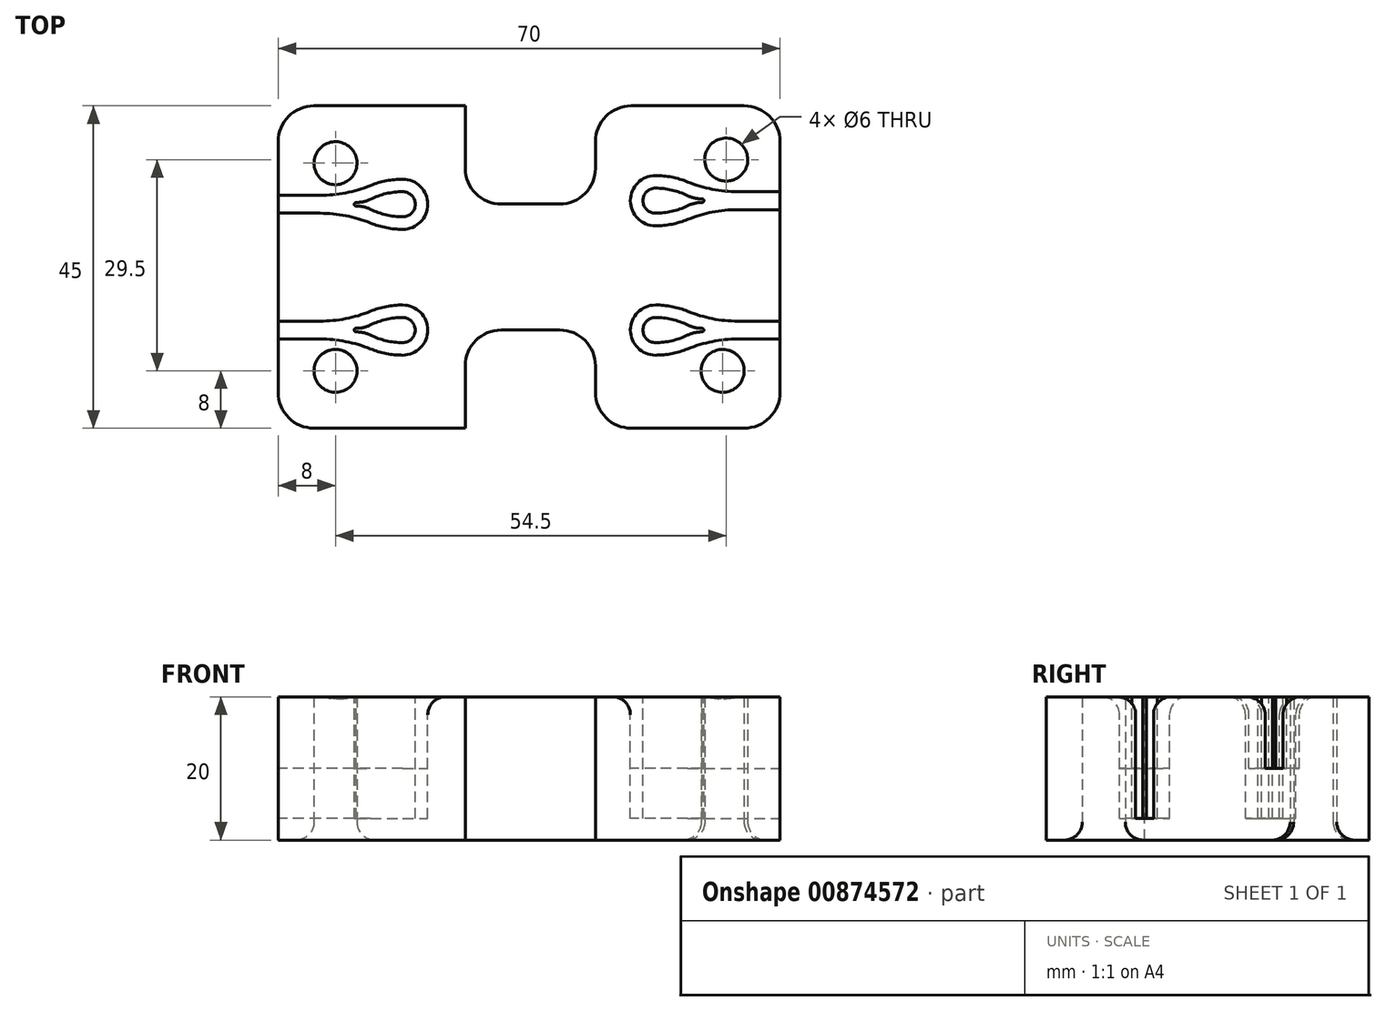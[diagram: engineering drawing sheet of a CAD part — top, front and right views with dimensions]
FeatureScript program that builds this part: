
annotation { "Feature Type Name" : "Feature", "Feature Type Description" : "" }
export const myFeature = defineFeature(function(context is Context, id is Id, definition is map)
    precondition{}
    {
        {
            var Q0;
            Q0=qCreatedBy(makeId("Top.planeOp"),FACE);
            var sketch = newSketch(context, id + "F0", { "sketchPlane" : qUnion([Q0])});
            skLineSegment(sketch, "E0.bottom", {"start": v(-35, 22.5) * mm, "end": v(35, 22.5) * mm});
            skLineSegment(sketch, "E0.top", {"start": v(-35, -22.5) * mm, "end": v(35, -22.5) * mm});
            skLineSegment(sketch, "E0.left", {"start": v(-35, 22.5) * mm, "end": v(-35, -22.5) * mm});
            skLineSegment(sketch, "E0.right", {"start": v(35, 22.5) * mm, "end": v(35, -22.5) * mm});
            skCircle(sketch, "E1", {"center": v(-27, 14.5) * mm, "radius": 3 * mm});
            skCircle(sketch, "E2", {"center": v(-27, -14.5) * mm, "radius": 3 * mm});
            skCircle(sketch, "E3", {"center": v(27, -14.5) * mm, "radius": 3 * mm});
            skCircle(sketch, "E4", {"center": v(27.5, 15) * mm, "radius": 3 * mm});
            skSolve(sketch);
        }
        {
            var Q0;
            Q0=makeQuery(id+"F0.imprint","IMPRINT",FACE,{"disambiguationData":[TD([[makeQuery(id+"F0.imprint","IMPRINT",EDGE,{"derivedFrom":sQuery(id+"F0.wireOp",EDGE,"E0.bottom")}),-1.0]])]});
            var Q1;
            Q1 = qSketchRegion(id + "F0", true);
            extrude(context, id + "F1", {"entities" : qUnion([Q0, Q1]), "depth" : 20 * mm, "offsetDistance" : 25 * mm});
        }
        {
            var Q0;
            Q0=makeQuery(id+"F1.opExtrude","CAP_FACE",FACE,{"disambiguationData":[OSD([sQuery(id+"F0.wireOp",EDGE,"E0.bottom"),sQuery(id+"F0.wireOp",EDGE,"E0.top"),sQuery(id+"F0.wireOp",EDGE,"E0.left"),sQuery(id+"F0.wireOp",EDGE,"E0.right"),sQuery(id+"F0.wireOp",EDGE,"E1"),sQuery(id+"F0.wireOp",EDGE,"E2"),sQuery(id+"F0.wireOp",EDGE,"E3"),sQuery(id+"F0.wireOp",EDGE,"E4")])],"isStart":false});
            var sketch = newSketch(context, id + "F2", { "sketchPlane" : qUnion([Q0])});
            skArc(sketch, "E5", {"start": v(17.63, 12.76) * mm, "mid": v(14.13, 9.26) * mm, "end": v(17.63, 5.76) * mm});
            skArc(sketch, "E6", {"start": v(17.63, 12.76) * mm, "mid": v(19.92, 12.54) * mm, "end": v(22.13, 11.88) * mm});
            skArc(sketch, "E7", {"start": v(22.13, 11.88) * mm, "mid": v(25.56, 10.86) * mm, "end": v(29.13, 10.51) * mm});
            skArc(sketch, "E8", {"start": v(17.63, 5.76) * mm, "mid": v(19.92, 5.98) * mm, "end": v(22.13, 6.64) * mm});
            skArc(sketch, "E9", {"start": v(22.13, 6.64) * mm, "mid": v(25.56, 7.67) * mm, "end": v(29.13, 8.01) * mm});
            skArc(sketch, "E10.0", {"start": v(17.63, 7.51) * mm, "mid": v(19.94, 7.78) * mm, "end": v(22.13, 8.56) * mm});
            skArc(sketch, "E10.1", {"start": v(17.63, 11.01) * mm, "mid": v(15.88, 9.26) * mm, "end": v(17.63, 7.51) * mm});
            skArc(sketch, "E10.4", {"start": v(17.63, 11.01) * mm, "mid": v(19.94, 10.75) * mm, "end": v(22.13, 9.96) * mm});
            skArc(sketch, "E11", {"start": v(22.13, 9.96) * mm, "mid": v(23.1, 9.62) * mm, "end": v(24.13, 9.51) * mm});
            skArc(sketch, "E12", {"start": v(22.13, 8.56) * mm, "mid": v(23.1, 8.9) * mm, "end": v(24.13, 9.01) * mm});
            skArc(sketch, "E13", {"start": v(24.13, 9.01) * mm, "mid": v(24.38, 9.26) * mm, "end": v(24.13, 9.51) * mm});
            skLineSegment(sketch, "E14.bottom", {"start": v(29.13, 10.51) * mm, "end": v(35, 10.51) * mm});
            skLineSegment(sketch, "E14.top", {"start": v(29.13, 8.01) * mm, "end": v(35, 8.01) * mm});
            skLineSegment(sketch, "E14.right", {"start": v(35, 10.51) * mm, "end": v(35, 8.01) * mm});
            skArc(sketch, "E15", {"start": v(17.63, -5.3) * mm, "mid": v(14.13, -8.8) * mm, "end": v(17.63, -12.3) * mm});
            skArc(sketch, "E16", {"start": v(17.63, -5.3) * mm, "mid": v(19.92, -5.52) * mm, "end": v(22.13, -6.18) * mm});
            skArc(sketch, "E17", {"start": v(22.13, -6.18) * mm, "mid": v(25.56, -7.2) * mm, "end": v(29.13, -7.55) * mm});
            skArc(sketch, "E18", {"start": v(17.63, -12.3) * mm, "mid": v(19.92, -12.08) * mm, "end": v(22.13, -11.42) * mm});
            skArc(sketch, "E19", {"start": v(22.13, -11.42) * mm, "mid": v(25.56, -10.4) * mm, "end": v(29.13, -10.05) * mm});
            skArc(sketch, "E20.0", {"start": v(17.63, -10.55) * mm, "mid": v(19.94, -10.29) * mm, "end": v(22.13, -9.5) * mm});
            skArc(sketch, "E20.1", {"start": v(17.63, -7.05) * mm, "mid": v(15.88, -8.8) * mm, "end": v(17.63, -10.55) * mm});
            skArc(sketch, "E20.4", {"start": v(17.63, -7.05) * mm, "mid": v(19.94, -7.32) * mm, "end": v(22.13, -8.1) * mm});
            skArc(sketch, "E21", {"start": v(22.13, -8.1) * mm, "mid": v(23.1, -8.44) * mm, "end": v(24.13, -8.55) * mm});
            skArc(sketch, "E22", {"start": v(22.13, -9.5) * mm, "mid": v(23.1, -9.16) * mm, "end": v(24.13, -9.05) * mm});
            skArc(sketch, "E23", {"start": v(24.13, -9.05) * mm, "mid": v(24.38, -8.8) * mm, "end": v(24.13, -8.55) * mm});
            skLineSegment(sketch, "E24.bottom", {"start": v(29.13, -7.55) * mm, "end": v(35, -7.55) * mm});
            skLineSegment(sketch, "E24.top", {"start": v(29.13, -10.05) * mm, "end": v(35, -10.05) * mm});
            skLineSegment(sketch, "E24.right", {"start": v(35, -7.55) * mm, "end": v(35, -10.05) * mm});
            skArc(sketch, "E25", {"start": v(-17.64, -12.3) * mm, "mid": v(-14.14, -8.8) * mm, "end": v(-17.64, -5.3) * mm});
            skArc(sketch, "E26", {"start": v(-17.64, -12.3) * mm, "mid": v(-19.93, -12.08) * mm, "end": v(-22.14, -11.42) * mm});
            skArc(sketch, "E27", {"start": v(-22.14, -11.42) * mm, "mid": v(-25.57, -10.4) * mm, "end": v(-29.14, -10.05) * mm});
            skArc(sketch, "E28", {"start": v(-17.64, -5.3) * mm, "mid": v(-19.93, -5.52) * mm, "end": v(-22.14, -6.18) * mm});
            skArc(sketch, "E29", {"start": v(-22.14, -6.18) * mm, "mid": v(-25.57, -7.2) * mm, "end": v(-29.14, -7.55) * mm});
            skArc(sketch, "E30.0", {"start": v(-17.64, -7.05) * mm, "mid": v(-19.95, -7.32) * mm, "end": v(-22.14, -8.1) * mm});
            skArc(sketch, "E30.1", {"start": v(-17.64, -10.55) * mm, "mid": v(-15.89, -8.8) * mm, "end": v(-17.64, -7.05) * mm});
            skArc(sketch, "E30.4", {"start": v(-17.64, -10.55) * mm, "mid": v(-19.95, -10.29) * mm, "end": v(-22.14, -9.5) * mm});
            skArc(sketch, "E31", {"start": v(-22.14, -9.5) * mm, "mid": v(-23.1, -9.16) * mm, "end": v(-24.13, -9.05) * mm});
            skArc(sketch, "E32", {"start": v(-22.14, -8.1) * mm, "mid": v(-23.11, -8.44) * mm, "end": v(-24.14, -8.55) * mm});
            skArc(sketch, "E33", {"start": v(-24.14, -8.55) * mm, "mid": v(-24.39, -8.8) * mm, "end": v(-24.13, -9.05) * mm});
            skLineSegment(sketch, "E34.bottom", {"start": v(-29.14, -10.05) * mm, "end": v(-35, -10.05) * mm});
            skLineSegment(sketch, "E34.top", {"start": v(-29.14, -7.55) * mm, "end": v(-35, -7.55) * mm});
            skLineSegment(sketch, "E34.right", {"start": v(-35, -10.05) * mm, "end": v(-35, -7.55) * mm});
            skArc(sketch, "E35", {"start": v(-17.63, 5.26) * mm, "mid": v(-14.13, 8.76) * mm, "end": v(-17.63, 12.26) * mm});
            skArc(sketch, "E36", {"start": v(-17.63, 5.26) * mm, "mid": v(-19.92, 5.48) * mm, "end": v(-22.13, 6.14) * mm});
            skArc(sketch, "E37", {"start": v(-22.13, 6.14) * mm, "mid": v(-25.56, 7.17) * mm, "end": v(-29.13, 7.51) * mm});
            skArc(sketch, "E38", {"start": v(-17.63, 12.26) * mm, "mid": v(-19.92, 12.04) * mm, "end": v(-22.13, 11.38) * mm});
            skArc(sketch, "E39", {"start": v(-22.13, 11.38) * mm, "mid": v(-25.56, 10.36) * mm, "end": v(-29.13, 10.01) * mm});
            skArc(sketch, "E40.0", {"start": v(-17.63, 10.51) * mm, "mid": v(-19.94, 10.25) * mm, "end": v(-22.13, 9.46) * mm});
            skArc(sketch, "E40.1", {"start": v(-17.63, 7.01) * mm, "mid": v(-15.88, 8.76) * mm, "end": v(-17.63, 10.51) * mm});
            skArc(sketch, "E40.4", {"start": v(-17.63, 7.01) * mm, "mid": v(-19.94, 7.28) * mm, "end": v(-22.13, 8.06) * mm});
            skArc(sketch, "E41", {"start": v(-22.13, 8.06) * mm, "mid": v(-23.1, 8.4) * mm, "end": v(-24.13, 8.51) * mm});
            skArc(sketch, "E42", {"start": v(-22.13, 9.46) * mm, "mid": v(-23.1, 9.12) * mm, "end": v(-24.13, 9.01) * mm});
            skArc(sketch, "E43", {"start": v(-24.13, 9.01) * mm, "mid": v(-24.38, 8.76) * mm, "end": v(-24.13, 8.51) * mm});
            skLineSegment(sketch, "E44.bottom", {"start": v(-29.13, 7.51) * mm, "end": v(-35, 7.51) * mm});
            skLineSegment(sketch, "E44.top", {"start": v(-29.13, 10.01) * mm, "end": v(-35, 10.01) * mm});
            skLineSegment(sketch, "E44.right", {"start": v(-35, 7.51) * mm, "end": v(-35, 10.01) * mm});
            skSolve(sketch);
        }
        {
            var Q0;
            {var subQ0=sQuery(id+"F0.wireOp",EDGE,"E0.top");var subQ1=sQuery(id+"F0.wireOp",EDGE,"E0.right");var subQ2=sQuery(id+"F0.wireOp",EDGE,"E0.bottom");var subQ3=sQuery(id+"F0.wireOp",EDGE,"E1");var subQ4=sQuery(id+"F0.wireOp",EDGE,"E2");var subQ5=sQuery(id+"F0.wireOp",EDGE,"E3");var subQ6=sQuery(id+"F0.wireOp",EDGE,"E4");var subQ7=sQuery(id+"F0.wireOp",EDGE,"E0.left");Q0=makeQuery(id+"FxYTic0K67xtiS1_1.boolean.opBoolean","SPLIT",FACE,{"disambiguationData":[TD([makeQuery(id+"F1.opExtrude","SWEPT_FACE",FACE,{"disambiguationData":[OSD([subQ2])]})])],"derivedFrom":makeQuery(id+"F1.opExtrude","CAP_FACE",FACE,{"disambiguationData":[OSD([subQ2,subQ0,subQ7,subQ1,subQ3,subQ4,subQ5,subQ6])],"isStart":false})});}
            var sketch = newSketch(context, id + "F3", { "sketchPlane" : qUnion([Q0])});
            skLineSegment(sketch, "E45.bottom", {"start": v(-8.9, 22.5) * mm, "end": v(9.26, 22.5) * mm});
            skLineSegment(sketch, "E45.top", {"start": v(-8.9, 8.8) * mm, "end": v(9.26, 8.8) * mm});
            skLineSegment(sketch, "E45.left", {"start": v(-8.9, 22.5) * mm, "end": v(-8.9, 8.8) * mm});
            skLineSegment(sketch, "E45.right", {"start": v(9.26, 22.5) * mm, "end": v(9.26, 8.8) * mm});
            skLineSegment(sketch, "E46.bottom", {"start": v(-8.9, -8.8) * mm, "end": v(9.26, -8.8) * mm});
            skLineSegment(sketch, "E46.top", {"start": v(-8.9, -22.5) * mm, "end": v(9.26, -22.5) * mm});
            skLineSegment(sketch, "E46.left", {"start": v(-8.9, -8.8) * mm, "end": v(-8.9, -22.5) * mm});
            skLineSegment(sketch, "E46.right", {"start": v(9.26, -8.8) * mm, "end": v(9.26, -22.5) * mm});
            skSolve(sketch);
        }
        {
            var Q0;
            Q0 = qSketchRegion(id + "F2", true);
            extrude(context, id + "F4", {"entities" : qUnion([Q0]), "operationType" : NewBodyOperationType.REMOVE, "oppositeDirection" : true, "depth" : 10 * mm, "offsetDistance" : 25 * mm});
        }
        {
            var Q0;
            Q0 = qSketchRegion(id + "F3", true);
            extrude(context, id + "F5", {"entities" : qUnion([Q0]), "operationType" : NewBodyOperationType.REMOVE, "oppositeDirection" : true, "depth" : 25 * mm, "offsetDistance" : 25 * mm});
        }
        {
            var Q0;
            Q0=makeQuery(id+"F5.boolean.opBoolean","COPY",EDGE,{"derivedFrom":makeQuery(id+"F5.opExtrude","SWEPT_EDGE",EDGE,{"disambiguationData":[OSD([sQuery(id+"F0.wireOp",EDGE,"E0.bottom"),sQuery(id+"F3.wireOp",EDGE,"E45.bottom"),sQuery(id+"F3.wireOp",EDGE,"E45.left")])]})});
            var Q1;
            Q1=makeQuery(id+"F5.boolean.opBoolean","COPY",EDGE,{"derivedFrom":makeQuery(id+"F5.opExtrude","SWEPT_EDGE",EDGE,{"disambiguationData":[OSD([sQuery(id+"F0.wireOp",EDGE,"E0.bottom"),sQuery(id+"F3.wireOp",EDGE,"E45.bottom"),sQuery(id+"F3.wireOp",EDGE,"E45.right")])]})});
            var Q2;
            Q2=makeQuery(id+"F1.opExtrude","SWEPT_EDGE",EDGE,{"disambiguationData":[OSD([sQuery(id+"F0.wireOp",EDGE,"E0.bottom"),sQuery(id+"F0.wireOp",EDGE,"E0.right")])]});
            var Q3;
            Q3=makeQuery(id+"F1.opExtrude","SWEPT_EDGE",EDGE,{"disambiguationData":[OSD([sQuery(id+"F0.wireOp",EDGE,"E0.top"),sQuery(id+"F0.wireOp",EDGE,"E0.right")])]});
            var Q4;
            Q4=makeQuery(id+"F5.boolean.opBoolean","COPY",EDGE,{"derivedFrom":makeQuery(id+"F5.opExtrude","SWEPT_EDGE",EDGE,{"disambiguationData":[OSD([sQuery(id+"F0.wireOp",EDGE,"E0.top"),sQuery(id+"F3.wireOp",EDGE,"E46.top"),sQuery(id+"F3.wireOp",EDGE,"E46.right")])]})});
            var Q5;
            Q5=makeQuery(id+"F5.boolean.opBoolean","COPY",EDGE,{"derivedFrom":makeQuery(id+"F5.opExtrude","SWEPT_EDGE",EDGE,{"disambiguationData":[OSD([sQuery(id+"F0.wireOp",EDGE,"E0.top"),sQuery(id+"F3.wireOp",EDGE,"E46.top"),sQuery(id+"F3.wireOp",EDGE,"E46.left")])]})});
            var Q6;
            Q6=makeQuery(id+"F1.opExtrude","SWEPT_EDGE",EDGE,{"disambiguationData":[OSD([sQuery(id+"F0.wireOp",EDGE,"E0.top"),sQuery(id+"F0.wireOp",EDGE,"E0.left")])]});
            var Q7;
            Q7=makeQuery(id+"F1.opExtrude","SWEPT_EDGE",EDGE,{"disambiguationData":[OSD([sQuery(id+"F0.wireOp",EDGE,"E0.bottom"),sQuery(id+"F0.wireOp",EDGE,"E0.left")])]});
            var Q8;
            Q8=makeQuery(id+"F5.boolean.opBoolean","COPY",EDGE,{"derivedFrom":makeQuery(id+"F5.opExtrude","SWEPT_EDGE",EDGE,{"disambiguationData":[OSD([sQuery(id+"F3.wireOp",EDGE,"E46.bottom"),sQuery(id+"F3.wireOp",EDGE,"E46.left")])]})});
            var Q9;
            Q9=makeQuery(id+"F5.boolean.opBoolean","COPY",EDGE,{"derivedFrom":makeQuery(id+"F5.opExtrude","SWEPT_EDGE",EDGE,{"disambiguationData":[OSD([sQuery(id+"F3.wireOp",EDGE,"E46.bottom"),sQuery(id+"F3.wireOp",EDGE,"E46.right")])]})});
            var Q10;
            Q10=makeQuery(id+"F5.boolean.opBoolean","COPY",EDGE,{"derivedFrom":makeQuery(id+"F5.opExtrude","SWEPT_EDGE",EDGE,{"disambiguationData":[OSD([sQuery(id+"F3.wireOp",EDGE,"E45.top"),sQuery(id+"F3.wireOp",EDGE,"E45.right")])]})});
            var Q11;
            Q11=makeQuery(id+"F5.boolean.opBoolean","COPY",EDGE,{"derivedFrom":makeQuery(id+"F5.opExtrude","SWEPT_EDGE",EDGE,{"disambiguationData":[OSD([sQuery(id+"F3.wireOp",EDGE,"E45.top"),sQuery(id+"F3.wireOp",EDGE,"E45.left")])]})});
            fillet(context, id + "F6", {"entities" : qUnion([Q0, Q1, Q2, Q3, Q4, Q5, Q6, Q7, Q8, Q9, Q10, Q11]), "radius" : 5 * mm, "tangentPropagation" : true, "allowEdgeOverflow" : false});
        }
        {
            var Q0;
            Q0=makeQuery(id+"F4.boolean.opBoolean","COPY",EDGE,{"derivedFrom":makeQuery(id+"F4.opExtrude","CAP_EDGE",EDGE,{"disambiguationData":[OSD([sQuery(id+"F2.wireOp",EDGE,"E44.top")])],"isStart":true})});
            var Q1;
            Q1=makeQuery(id+"F4.boolean.opBoolean","COPY",EDGE,{"derivedFrom":makeQuery(id+"F4.opExtrude","CAP_EDGE",EDGE,{"disambiguationData":[OSD([sQuery(id+"F2.wireOp",EDGE,"E14.bottom")])],"isStart":true})});
            var Q2;
            Q2=makeQuery(id+"F4.boolean.opBoolean","COPY",EDGE,{"derivedFrom":makeQuery(id+"F4.opExtrude","CAP_EDGE",EDGE,{"disambiguationData":[OSD([sQuery(id+"F2.wireOp",EDGE,"E24.bottom")])],"isStart":true})});
            var Q3;
            Q3=makeQuery(id+"F4.boolean.opBoolean","COPY",EDGE,{"derivedFrom":makeQuery(id+"F4.opExtrude","CAP_EDGE",EDGE,{"disambiguationData":[OSD([sQuery(id+"F2.wireOp",EDGE,"E28")])],"isStart":true})});
            fillet(context, id + "F7", {"entities" : qUnion([Q0, Q1, Q2, Q3]), "radius" : 2.5 * mm, "tangentPropagation" : true, "allowEdgeOverflow" : false});
        }
        {
            var Q0;
            Q0=makeQuery(id+"F1.opExtrude","CAP_EDGE",EDGE,{"disambiguationData":[OSD([sQuery(id+"F0.wireOp",EDGE,"E1")])],"isStart":true});
            var Q1;
            Q1=makeQuery(id+"F1.opExtrude","CAP_EDGE",EDGE,{"disambiguationData":[OSD([sQuery(id+"F0.wireOp",EDGE,"E2")])],"isStart":true});
            var Q2;
            Q2=makeQuery(id+"F1.opExtrude","CAP_EDGE",EDGE,{"disambiguationData":[OSD([sQuery(id+"F0.wireOp",EDGE,"E3")])],"isStart":true});
            var Q3;
            Q3=makeQuery(id+"F1.opExtrude","CAP_EDGE",EDGE,{"disambiguationData":[OSD([sQuery(id+"F0.wireOp",EDGE,"E4")])],"isStart":true});
            fillet(context, id + "F8", {"entities" : qUnion([Q0, Q1, Q2, Q3]), "radius" : 2.5 * mm, "tangentPropagation" : true, "allowEdgeOverflow" : false});
        }
        {
            var Q0;
            {var subQ5=sQuery(id+"F0.wireOp",EDGE,"E0.left");var subQ6=sQuery(id+"F0.wireOp",EDGE,"E0.top");Q0=makeQuery(id+"F5.boolean.opBoolean","SPLIT",FACE,{"disambiguationData":[TD([makeQuery(id+"F1.opExtrude","SWEPT_FACE",FACE,{"disambiguationData":[OSD([subQ5])]})])],"derivedFrom":makeQuery(id+"F1.opExtrude","SWEPT_FACE",FACE,{"disambiguationData":[OSD([subQ6])]})});}
            var sketch = newSketch(context, id + "F9", { "sketchPlane" : qUnion([Q0])});
            skArc(sketch, "E47", {"start": v(14.51, 0) * mm, "mid": v(0.3, 4.59) * mm, "end": v(-13.9, 0) * mm});
            skLineSegment(sketch, "E48", {"start": v(-13.9, 0) * mm, "end": v(14.51, 0) * mm});
            skSolve(sketch);
        }
        {
            var Q0;
            Q0=makeQuery(id+"F4.boolean.opBoolean","COPY",FACE,{"derivedFrom":makeQuery(id+"F4.opExtrude","CAP_FACE",FACE,{"disambiguationData":[OSD([sQuery(id+"F2.wireOp",EDGE,"E35"),sQuery(id+"F2.wireOp",EDGE,"E36"),sQuery(id+"F2.wireOp",EDGE,"E37"),sQuery(id+"F2.wireOp",EDGE,"E38"),sQuery(id+"F2.wireOp",EDGE,"E39"),sQuery(id+"F2.wireOp",EDGE,"E40.0"),sQuery(id+"F2.wireOp",EDGE,"E40.1"),sQuery(id+"F2.wireOp",EDGE,"E40.4"),sQuery(id+"F2.wireOp",EDGE,"E41"),sQuery(id+"F2.wireOp",EDGE,"E42"),sQuery(id+"F2.wireOp",EDGE,"E43"),sQuery(id+"F2.wireOp",EDGE,"E44.bottom"),sQuery(id+"F2.wireOp",EDGE,"E44.top"),sQuery(id+"F2.wireOp",EDGE,"E44.right")])],"isStart":false})});
            var Q1;
            Q1=makeQuery(id+"F4.boolean.opBoolean","COPY",FACE,{"derivedFrom":makeQuery(id+"F4.opExtrude","CAP_FACE",FACE,{"disambiguationData":[OSD([sQuery(id+"F2.wireOp",EDGE,"E15"),sQuery(id+"F2.wireOp",EDGE,"E16"),sQuery(id+"F2.wireOp",EDGE,"E17"),sQuery(id+"F2.wireOp",EDGE,"E18"),sQuery(id+"F2.wireOp",EDGE,"E19"),sQuery(id+"F2.wireOp",EDGE,"E20.0"),sQuery(id+"F2.wireOp",EDGE,"E20.1"),sQuery(id+"F2.wireOp",EDGE,"E20.4"),sQuery(id+"F2.wireOp",EDGE,"E21"),sQuery(id+"F2.wireOp",EDGE,"E22"),sQuery(id+"F2.wireOp",EDGE,"E23"),sQuery(id+"F2.wireOp",EDGE,"E24.bottom"),sQuery(id+"F2.wireOp",EDGE,"E24.top"),sQuery(id+"F2.wireOp",EDGE,"E24.right")])],"isStart":false})});
            extrude(context, id + "F10", {"entities" : qUnion([Q0, Q1]), "operationType" : NewBodyOperationType.REMOVE, "oppositeDirection" : true, "depth" : 7 * mm, "offsetDistance" : 25 * mm});
        }
    });
